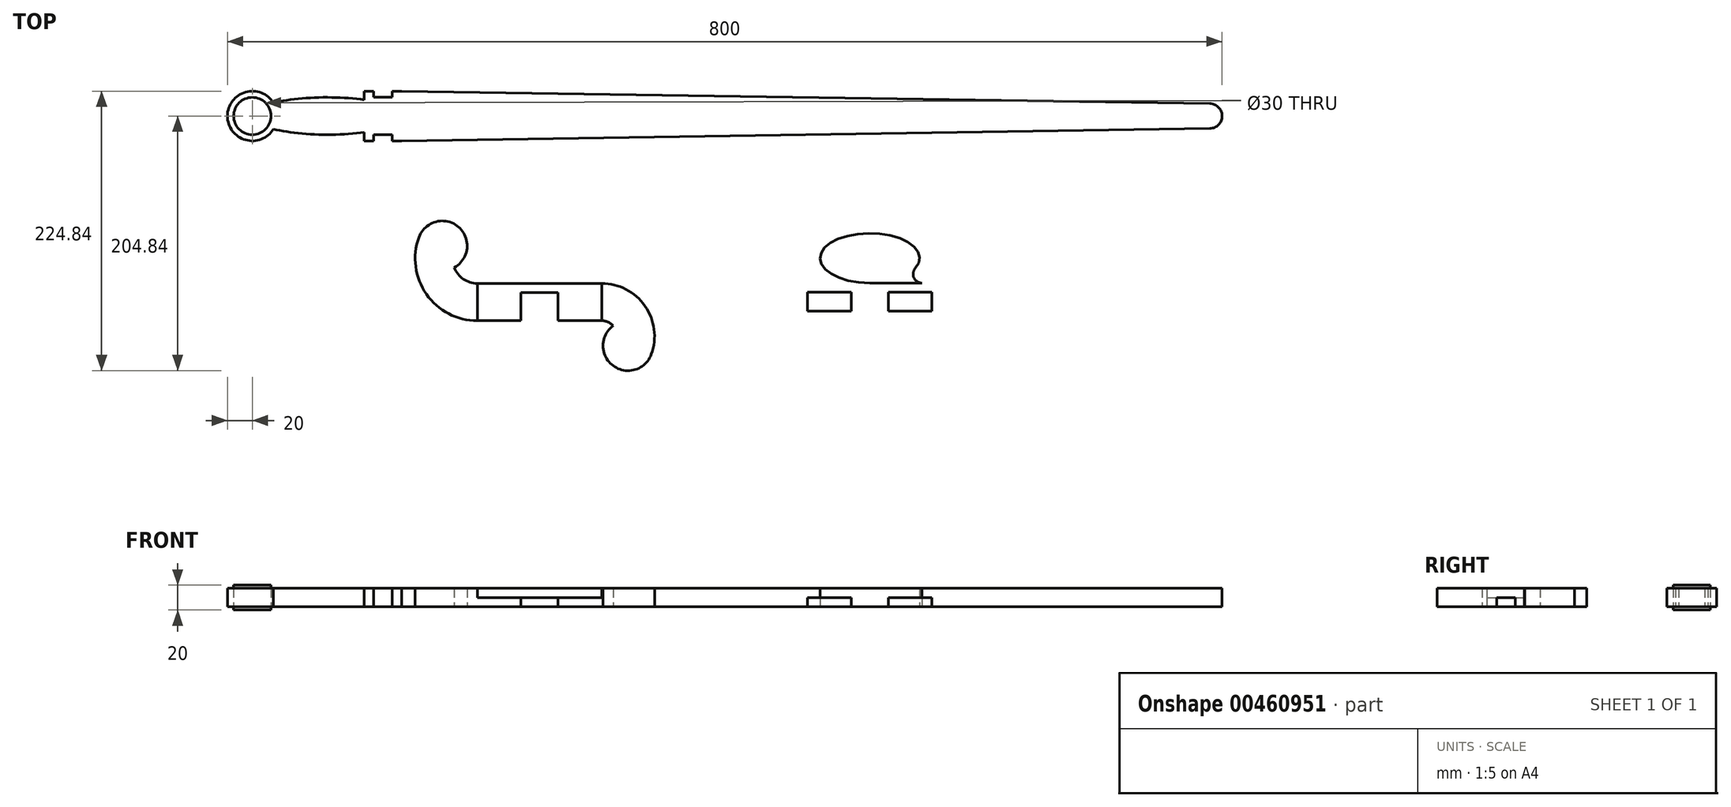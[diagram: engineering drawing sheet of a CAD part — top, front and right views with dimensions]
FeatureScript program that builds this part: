
annotation { "Feature Type Name" : "Feature", "Feature Type Description" : "" }
export const myFeature = defineFeature(function(context is Context, id is Id, definition is map)
    precondition{}
    {
        {
            var Q0;
            Q0=qCreatedBy(makeId("Top.planeOp"),FACE);
            var sketch = newSketch(context, id + "F0", { "sketchPlane" : qUnion([Q0])});
            skLineSegment(sketch, "E0", {"start": v(0, 0) * mm, "end": v(770, 0) * mm, "construction": true});
            skCircle(sketch, "E1", {"center": v(0, 0) * mm, "radius": 20 * mm});
            skLineSegment(sketch, "E2", {"start": v(60, 0) * mm, "end": v(60, 15) * mm, "construction": true});
            skEllipse(sketch, "E3", {"center": v(60, 0) * mm, "majorRadius": 60 * mm, "minorRadius": 15 * mm, "majorAxis": v(-1, 0)});
            skLineSegment(sketch, "E4.bottom", {"start": v(120, -20) * mm, "end": v(112.5, -20) * mm});
            skLineSegment(sketch, "E4.top", {"start": v(120, 20) * mm, "end": v(112.5, 20) * mm});
            skLineSegment(sketch, "E4.left", {"start": v(120, -20) * mm, "end": v(120, 20) * mm, "construction": true});
            skLineSegment(sketch, "E4.right", {"start": v(90, -20) * mm, "end": v(90, 20) * mm});
            skPoint(sketch, "E4.middle", {"position": v(105, 0) * mm});
            skPoint(sketch, "E4.cornerSnap0", {"position": v(120, 0) * mm});
            skCircle(sketch, "E5", {"center": v(770, 0) * mm, "radius": 10 * mm});
            skLineSegment(sketch, "E6", {"start": v(120, 20) * mm, "end": v(770.15, 10) * mm});
            skLineSegment(sketch, "E7", {"start": v(120, -20) * mm, "end": v(770.15, -10) * mm});
            skLineSegment(sketch, "E8", {"start": v(-20, 0) * mm, "end": v(-20, 37.29) * mm, "construction": true});
            skLineSegment(sketch, "E9", {"start": v(780, 0) * mm, "end": v(780, 49.93) * mm, "construction": true});
            skLineSegment(sketch, "E10.bottom", {"start": v(112.5, 15) * mm, "end": v(97.5, 15) * mm});
            skLineSegment(sketch, "E10.top", {"start": v(112.5, -15) * mm, "end": v(97.5, -15) * mm});
            skLineSegment(sketch, "E10.left", {"start": v(112.5, 15) * mm, "end": v(112.5, -15) * mm, "construction": true});
            skLineSegment(sketch, "E10.right", {"start": v(97.5, 15) * mm, "end": v(97.5, -15) * mm, "construction": true});
            skLineSegment(sketch, "E11", {"start": v(97.5, -15) * mm, "end": v(97.5, -20) * mm});
            skLineSegment(sketch, "E12", {"start": v(112.5, -15) * mm, "end": v(112.5, -20) * mm});
            skLineSegment(sketch, "E13", {"start": v(97.5, 15) * mm, "end": v(97.5, 20) * mm});
            skLineSegment(sketch, "E14", {"start": v(112.5, 15) * mm, "end": v(112.5, 20) * mm});
            skLineSegment(sketch, "E15", {"start": v(97.5, 20) * mm, "end": v(90, 20) * mm});
            skLineSegment(sketch, "E16", {"start": v(112.5, 20) * mm, "end": v(97.5, 20) * mm, "construction": true});
            skLineSegment(sketch, "E17", {"start": v(97.5, -20) * mm, "end": v(90, -20) * mm});
            skLineSegment(sketch, "E18", {"start": v(112.5, -20) * mm, "end": v(97.5, -20) * mm, "construction": true});
            skLineSegment(sketch, "E19.bottom", {"start": v(181, -149.65) * mm, "end": v(281, -149.65) * mm, "construction": true});
            skLineSegment(sketch, "E19.top", {"start": v(181, -134.65) * mm, "end": v(281, -134.65) * mm});
            skLineSegment(sketch, "E19.left", {"start": v(181, -149.65) * mm, "end": v(181, -134.65) * mm});
            skLineSegment(sketch, "E19.right", {"start": v(281, -149.65) * mm, "end": v(281, -134.65) * mm});
            skLineSegment(sketch, "E20.bottom", {"start": v(281, -142.15) * mm, "end": v(181, -142.15) * mm});
            skLineSegment(sketch, "E20.top", {"start": v(281, -157.15) * mm, "end": v(181, -157.15) * mm, "construction": true});
            skLineSegment(sketch, "E20.left", {"start": v(281, -142.15) * mm, "end": v(281, -164.65) * mm});
            skLineSegment(sketch, "E20.right", {"start": v(181, -142.15) * mm, "end": v(181, -164.65) * mm});
            skArc(sketch, "E21", {"start": v(181, -134.65) * mm, "mid": v(169.74, -131.17) * mm, "end": v(162.39, -121.95) * mm});
            skLineSegment(sketch, "E22", {"start": v(181, -114.65) * mm, "end": v(162.39, -121.95) * mm, "construction": true});
            skLineSegment(sketch, "E23", {"start": v(130.77, -96.36) * mm, "end": v(181, -114.65) * mm, "construction": true});
            skLineSegment(sketch, "E24.bottom", {"start": v(246, -157.15) * mm, "end": v(216, -157.15) * mm});
            skLineSegment(sketch, "E24.top", {"start": v(246, -142.15) * mm, "end": v(216, -142.15) * mm});
            skLineSegment(sketch, "E24.left", {"start": v(246, -164.65) * mm, "end": v(246, -142.15) * mm});
            skLineSegment(sketch, "E24.right", {"start": v(216, -164.65) * mm, "end": v(216, -142.15) * mm});
            skPoint(sketch, "E24.middle", {"position": v(231, -149.65) * mm});
            skArc(sketch, "E25", {"start": v(281, -134.65) * mm, "mid": v(315.82, -152.77) * mm, "end": v(320.94, -191.68) * mm});
            skLineSegment(sketch, "E26", {"start": v(281, -177.15) * mm, "end": v(320.94, -191.68) * mm, "construction": true});
            skLineSegment(sketch, "E27.bottom", {"start": v(546.61, -149.34) * mm, "end": v(446.61, -149.34) * mm});
            skLineSegment(sketch, "E27.top", {"start": v(546.61, -134.34) * mm, "end": v(446.61, -134.34) * mm});
            skLineSegment(sketch, "E27.left", {"start": v(546.61, -156.84) * mm, "end": v(546.61, -134.34) * mm});
            skLineSegment(sketch, "E27.right", {"start": v(446.61, -156.84) * mm, "end": v(446.61, -134.34) * mm});
            skPoint(sketch, "E27.middle", {"position": v(496.61, -141.84) * mm});
            skLineSegment(sketch, "E28.bottom", {"start": v(546.61, -141.84) * mm, "end": v(446.61, -141.84) * mm});
            skLineSegment(sketch, "E28.top", {"start": v(527.84, -126.84) * mm, "end": v(465.39, -126.84) * mm});
            skLineSegment(sketch, "E28.left", {"start": v(546.61, -141.84) * mm, "end": v(546.61, -134.34) * mm});
            skLineSegment(sketch, "E28.right", {"start": v(446.61, -141.84) * mm, "end": v(446.61, -134.34) * mm});
            skPoint(sketch, "E28.middle", {"position": v(496.61, -134.34) * mm});
            skLineSegment(sketch, "E29", {"start": v(496.61, -134.34) * mm, "end": v(496.61, -114.34) * mm, "construction": true});
            skPoint(sketch, "E29.endSnap0", {"position": v(496.61, -126.84) * mm});
            skLineSegment(sketch, "E30", {"start": v(496.61, -114.34) * mm, "end": v(536.61, -114.34) * mm, "construction": true});
            skEllipse(sketch, "E31", {"center": v(496.61, -114.34) * mm, "majorRadius": 20 * mm, "minorRadius": 40 * mm, "majorAxis": v(0, -1)});
            skLineSegment(sketch, "E32.bottom", {"start": v(511.61, -134.34) * mm, "end": v(481.61, -134.34) * mm});
            skLineSegment(sketch, "E32.top", {"start": v(511.61, -149.34) * mm, "end": v(481.61, -149.34) * mm});
            skLineSegment(sketch, "E32.left", {"start": v(511.61, -134.34) * mm, "end": v(511.61, -156.84) * mm});
            skLineSegment(sketch, "E32.right", {"start": v(481.61, -134.34) * mm, "end": v(481.61, -156.84) * mm});
            skPoint(sketch, "E33.orphan", {"position": v(446.61, -126.84) * mm});
            skPoint(sketch, "E34.orphan", {"position": v(546.61, -126.84) * mm});
            skLineSegment(sketch, "E35", {"start": v(453.57, -122.34) * mm, "end": v(546.39, -122.34) * mm, "construction": true});
            skLineSegment(sketch, "E36", {"start": v(459.95, -122.34) * mm, "end": v(458.64, -120.84) * mm, "construction": true});
            skLineSegment(sketch, "E37", {"start": v(533.27, -122.34) * mm, "end": v(542.09, -112.24) * mm, "construction": true});
            skArc(sketch, "E38", {"start": v(459.95, -122.34) * mm, "mid": v(461.09, -130.1) * mm, "end": v(454.5, -134.34) * mm});
            skArc(sketch, "E39", {"start": v(533.27, -122.34) * mm, "mid": v(532.13, -130.1) * mm, "end": v(538.73, -134.34) * mm});
            skLineSegment(sketch, "E40.MirrorCS", {"start": v(181, -164.65) * mm, "end": v(281, -164.65) * mm});
            skArc(sketch, "E41", {"start": v(181, -164.65) * mm, "mid": v(140.05, -143.33) * mm, "end": v(134.02, -97.55) * mm});
            skArc(sketch, "E42", {"start": v(134.02, -97.55) * mm, "mid": v(165.86, -89.22) * mm, "end": v(162.39, -121.95) * mm});
            skLineSegment(sketch, "E43", {"start": v(281, -177.15) * mm, "end": v(290.27, -168.75) * mm, "construction": true});
            skArc(sketch, "E44", {"start": v(281, -164.65) * mm, "mid": v(286.07, -165.72) * mm, "end": v(290.27, -168.75) * mm});
            skArc(sketch, "E45", {"start": v(320.94, -191.68) * mm, "mid": v(290.18, -200.86) * mm, "end": v(290.27, -168.75) * mm});
            skLineSegment(sketch, "E46.MirrorCS", {"start": v(546.61, -156.84) * mm, "end": v(446.61, -156.84) * mm});
            skCircle(sketch, "E47", {"center": v(0, 0) * mm, "radius": 15 * mm});
            skSolve(sketch);
        }
        {
            var Q0;
            Q0=makeQuery(id+"F0.imprint","IMPRINT",FACE,{"disambiguationData":[TD([[makeQuery(id+"F0.imprint","IMPRINT",EDGE,{"derivedFrom":sQuery(id+"F0.wireOp",EDGE,"E4.bottom")}),-1.0]])]});
            var Q1;
            {var subQ0=sQuery(id+"F0.wireOp",EDGE,"E4.right");var subQ1=sQuery(id+"F0.wireOp",EDGE,"E3");var subQ2=makeQuery(id+"F0.imprint","INTERSECT",VERTEX,{"disambiguationData":[OD(0.0)],"derivedFrom":[subQ1,subQ0]});Q1=makeQuery(id+"F0.imprint","IMPRINT",FACE,{"disambiguationData":[TD([[makeQuery(id+"F0.imprint","IMPRINT",EDGE,{"disambiguationData":[TD([[subQ2,-1.0]])],"derivedFrom":subQ1}),1.0]])]});}
            var Q2;
            {var subQ0=sQuery(id+"F0.wireOp",EDGE,"E3");var subQ1=sQuery(id+"F0.wireOp",EDGE,"E1");var subQ2=makeQuery(id+"F0.imprint","INTERSECT",VERTEX,{"disambiguationData":[OD(0.0)],"derivedFrom":[subQ1,subQ0]});Q2=makeQuery(id+"F0.imprint","IMPRINT",FACE,{"disambiguationData":[TD([[makeQuery(id+"F0.imprint","IMPRINT",EDGE,{"disambiguationData":[TD([[subQ2,-1.0]])],"derivedFrom":subQ1}),1.0]])]});}
            var Q3;
            {var subQ0=sQuery(id+"F0.wireOp",EDGE,"E3");var subQ1=sQuery(id+"F0.wireOp",EDGE,"E1");var subQ2=makeQuery(id+"F0.imprint","INTERSECT",VERTEX,{"disambiguationData":[OD(0.0)],"derivedFrom":[subQ1,subQ0]});Q3=makeQuery(id+"F0.imprint","IMPRINT",FACE,{"disambiguationData":[TD([[makeQuery(id+"F0.imprint","IMPRINT",EDGE,{"disambiguationData":[TD([[subQ2,1.0]])],"derivedFrom":subQ1}),1.0]])]});}
            var Q4;
            {var subQ0=sQuery(id+"F0.wireOp",EDGE,"E3");var subQ1=sQuery(id+"F0.wireOp",EDGE,"E1");var subQ2=makeQuery(id+"F0.imprint","INTERSECT",VERTEX,{"disambiguationData":[OD(0.0)],"derivedFrom":[subQ1,subQ0]});Q4=makeQuery(id+"F0.imprint","IMPRINT",FACE,{"disambiguationData":[TD([[makeQuery(id+"F0.imprint","IMPRINT",EDGE,{"disambiguationData":[TD([[subQ2,-1.0]])],"derivedFrom":subQ1}),-1.0]])]});}
            var Q5;
            {var subQ0=sQuery(id+"F0.wireOp",EDGE,"E5");var subQ1=makeQuery(id+"F0.imprint","INTERSECT",VERTEX,{"derivedFrom":[subQ0,sQuery(id+"F0.wireOp",EDGE,"E6")]});Q5=makeQuery(id+"F0.imprint","IMPRINT",FACE,{"disambiguationData":[TD([[makeQuery(id+"F0.imprint","IMPRINT",EDGE,{"disambiguationData":[TD([[subQ1,-1.0]])],"derivedFrom":subQ0}),1.0]])]});}
            var Q6;
            {var subQ1=sQuery(id+"F0.wireOp",EDGE,"01afa8eb-54a4-497e-899c-582eb727d7de");Q6=makeQuery(id+"F0.imprint","IMPRINT",FACE,{"disambiguationData":[TD([[makeQuery(id+"F0.imprint","IMPRINT",EDGE,{"derivedFrom":subQ1}),-1.0]])]});}
            var Q7;
            Q7=makeQuery(id+"F0.imprint","IMPRINT",FACE,{"disambiguationData":[TD([[makeQuery(id+"F0.imprint","IMPRINT",EDGE,{"derivedFrom":sQuery(id+"F0.wireOp",EDGE,"81f064dc-e89b-471e-82f6-2df51cb97110.0")}),-1.0]])]});
            var Q8;
            {var subQ2=sQuery(id+"F0.wireOp",EDGE,"E19.left");Q8=makeQuery(id+"F0.imprint","IMPRINT",FACE,{"disambiguationData":[TD([[makeQuery(id+"F0.imprint","IMPRINT",EDGE,{"derivedFrom":subQ2}),1.0]])]});}
            var Q9;
            {var subQ2=sQuery(id+"F0.wireOp",EDGE,"E19.right");Q9=makeQuery(id+"F0.imprint","IMPRINT",FACE,{"disambiguationData":[TD([[makeQuery(id+"F0.imprint","IMPRINT",EDGE,{"derivedFrom":subQ2}),-1.0]])]});}
            var Q10;
            {var subQ0=sQuery(id+"F0.wireOp",EDGE,"E31");var subQ1=sQuery(id+"F0.wireOp",EDGE,"E28.top");var subQ2=makeQuery(id+"F0.imprint","INTERSECT",VERTEX,{"derivedFrom":[subQ1,subQ0,sQuery(id+"F0.wireOp",EDGE,"nQVR4g7v-FuoA-UHvy-gGBo-ylVEHgYElvSI")]});Q10=makeQuery(id+"F0.imprint","IMPRINT",FACE,{"disambiguationData":[TD([[makeQuery(id+"F0.imprint","IMPRINT",EDGE,{"disambiguationData":[TD([[subQ2,1.0]])],"derivedFrom":subQ1}),-1.0]])]});}
            var Q11;
            {var subQ0=sQuery(id+"F0.wireOp",EDGE,"E31");var subQ4=makeQuery(id+"F0.imprint","INTERSECT",VERTEX,{"derivedFrom":[sQuery(id+"F0.wireOp",EDGE,"E27.top"),subQ0]});Q11=makeQuery(id+"F0.imprint","IMPRINT",FACE,{"disambiguationData":[TD([[makeQuery(id+"F0.imprint","IMPRINT",EDGE,{"disambiguationData":[TD([[subQ4,1.0]])],"derivedFrom":subQ0}),1.0]])]});}
            var Q12;
            {var subQ3=sQuery(id+"F0.wireOp",EDGE,"9fee9edf-713e-429d-bc3d-18e314127ecd");Q12=makeQuery(id+"F0.imprint","IMPRINT",FACE,{"disambiguationData":[TD([[makeQuery(id+"F0.imprint","IMPRINT",EDGE,{"derivedFrom":subQ3}),-1.0]])]});}
            var Q13;
            {var subQ3=sQuery(id+"F0.wireOp",EDGE,"f64fa683-d323-478d-b828-0c1e24b545ef");Q13=makeQuery(id+"F0.imprint","IMPRINT",FACE,{"disambiguationData":[TD([[makeQuery(id+"F0.imprint","IMPRINT",EDGE,{"derivedFrom":subQ3}),1.0]])]});}
            var Q14;
            {var subQ3=sQuery(id+"F0.wireOp",EDGE,"8bb32b30-6a59-4a8c-b171-4b0a19f8ac91");Q14=makeQuery(id+"F0.imprint","IMPRINT",FACE,{"disambiguationData":[TD([[makeQuery(id+"F0.imprint","IMPRINT",EDGE,{"derivedFrom":subQ3}),1.0]])]});}
            var Q15;
            {var subQ3=sQuery(id+"F0.wireOp",EDGE,"c7db875d-1e1a-4694-8620-a06d6eaf2f13");Q15=makeQuery(id+"F0.imprint","IMPRINT",FACE,{"disambiguationData":[TD([[makeQuery(id+"F0.imprint","IMPRINT",EDGE,{"derivedFrom":subQ3}),-1.0]])]});}
            var Q16;
            {var subQ0=sQuery(id+"F0.wireOp",EDGE,"E28.top");Q16=makeQuery(id+"F0.imprint","IMPRINT",FACE,{"disambiguationData":[TD([[makeQuery(id+"F0.imprint","IMPRINT",EDGE,{"derivedFrom":subQ0}),1.0]])]});}
            var Q17;
            {var subQ4=sQuery(id+"F0.wireOp",EDGE,"E38");Q17=makeQuery(id+"F0.imprint","IMPRINT",FACE,{"disambiguationData":[TD([[makeQuery(id+"F0.imprint","IMPRINT",EDGE,{"derivedFrom":subQ4}),1.0]])]});}
            var Q18;
            {var subQ2=sQuery(id+"F0.wireOp",EDGE,"E39");Q18=makeQuery(id+"F0.imprint","IMPRINT",FACE,{"disambiguationData":[TD([[makeQuery(id+"F0.imprint","IMPRINT",EDGE,{"derivedFrom":subQ2}),-1.0]])]});}
            extrude(context, id + "F1", {"entities" : qUnion([Q0, Q1, Q2, Q3, Q4, Q5, Q6, Q7, Q8, Q9, Q10, Q11, Q12, Q13, Q14, Q15, Q16, Q17, Q18]), "depth" : 15 * mm});
        }
        {
            var Q0;
            {var subQ0=sQuery(id+"F0.wireOp",EDGE,"E28.left");Q0=makeQuery(id+"F0.imprint","IMPRINT",FACE,{"disambiguationData":[TD([[makeQuery(id+"F0.imprint","IMPRINT",EDGE,{"derivedFrom":subQ0}),1.0]])]});}
            var Q1;
            {var subQ0=sQuery(id+"F0.wireOp",EDGE,"E28.right");Q1=makeQuery(id+"F0.imprint","IMPRINT",FACE,{"disambiguationData":[TD([[makeQuery(id+"F0.imprint","IMPRINT",EDGE,{"derivedFrom":subQ0}),-1.0]])]});}
            var Q2;
            {var subQ0=sQuery(id+"F0.wireOp",EDGE,"E27.left");Q2=makeQuery(id+"F0.imprint","IMPRINT",FACE,{"disambiguationData":[TD([[makeQuery(id+"F0.imprint","IMPRINT",EDGE,{"derivedFrom":subQ0}),1.0]])]});}
            var Q3;
            {var subQ0=sQuery(id+"F0.wireOp",EDGE,"E27.right");Q3=makeQuery(id+"F0.imprint","IMPRINT",FACE,{"disambiguationData":[TD([[makeQuery(id+"F0.imprint","IMPRINT",EDGE,{"derivedFrom":subQ0}),-1.0]])]});}
            extrude(context, id + "F2", {"entities" : qUnion([Q0, Q1, Q2, Q3]), "operationType" : NewBodyOperationType.ADD, "depth" : 7.5 * mm});
        }
        {
            var Q0;
            {var subQ4=sQuery(id+"F0.wireOp",EDGE,"E20.left");var subQ6=makeQuery(id+"F0.imprint","IMPRINT",VERTEX,{"derivedFrom":subQ4});Q0=makeQuery(id+"F0.imprint","IMPRINT",FACE,{"disambiguationData":[TD([[makeQuery(id+"F0.imprint","IMPRINT",EDGE,{"disambiguationData":[TD([[subQ6,1.0]])],"derivedFrom":subQ4}),-1.0]])]});}
            var Q1;
            {var subQ4=sQuery(id+"F0.wireOp",EDGE,"E20.right");var subQ6=makeQuery(id+"F0.imprint","IMPRINT",VERTEX,{"derivedFrom":subQ4});Q1=makeQuery(id+"F0.imprint","IMPRINT",FACE,{"disambiguationData":[TD([[makeQuery(id+"F0.imprint","IMPRINT",EDGE,{"disambiguationData":[TD([[subQ6,1.0]])],"derivedFrom":subQ4}),1.0]])]});}
            var Q2;
            Q2=makeQuery(id+"F0.imprint","IMPRINT",FACE,{"disambiguationData":[TD([[makeQuery(id+"F0.imprint","IMPRINT",EDGE,{"derivedFrom":sQuery(id+"F0.wireOp",EDGE,"E19.top")}),-1.0]])]});
            extrude(context, id + "F3", {"entities" : qUnion([Q0, Q1, Q2]), "operationType" : NewBodyOperationType.ADD, "depth" : 7.5 * mm});
        }
        {
            var Q0;
            {var subQ0=sQuery(id+"F0.wireOp",EDGE,"E47");var subQ1=sQuery(id+"F0.wireOp",EDGE,"E3");var subQ2=makeQuery(id+"F0.imprint","INTERSECT",VERTEX,{"disambiguationData":[OD(0.0)],"derivedFrom":[subQ1,subQ0]});Q0=makeQuery(id+"F0.imprint","IMPRINT",FACE,{"disambiguationData":[TD([[makeQuery(id+"F0.imprint","IMPRINT",EDGE,{"disambiguationData":[TD([[subQ2,1.0]])],"derivedFrom":subQ1}),-1.0]])]});}
            var Q1;
            {var subQ0=sQuery(id+"F0.wireOp",EDGE,"E47");var subQ1=sQuery(id+"F0.wireOp",EDGE,"E3");var subQ2=makeQuery(id+"F0.imprint","INTERSECT",VERTEX,{"disambiguationData":[OD(0.0)],"derivedFrom":[subQ1,subQ0]});Q1=makeQuery(id+"F0.imprint","IMPRINT",FACE,{"disambiguationData":[TD([[makeQuery(id+"F0.imprint","IMPRINT",EDGE,{"disambiguationData":[TD([[subQ2,1.0]])],"derivedFrom":subQ1}),1.0]])]});}
            extrude(context, id + "F4", {"entities" : qUnion([Q0, Q1]), "depth" : 17.5 * mm, "hasSecondDirection" : true, "secondDirectionOppositeDirection" : true, "secondDirectionDepth" : 2.5 * mm});
        }
    });
